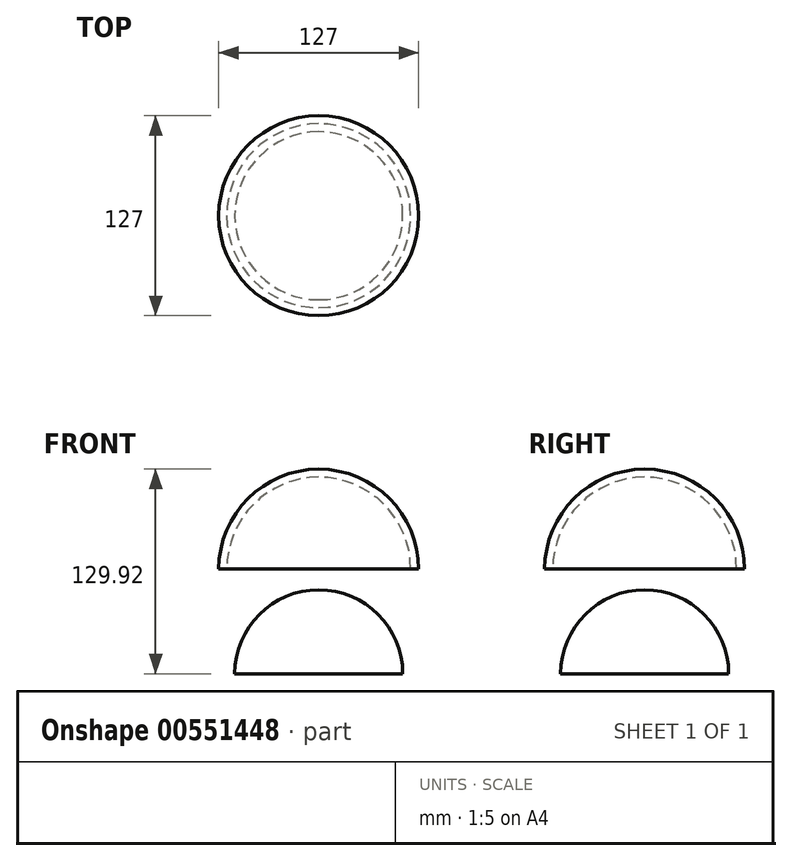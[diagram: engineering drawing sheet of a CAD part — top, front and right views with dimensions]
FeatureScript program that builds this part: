
annotation { "Feature Type Name" : "Feature", "Feature Type Description" : "" }
export const myFeature = defineFeature(function(context is Context, id is Id, definition is map)
    precondition{}
    {
        {
            var Q0;
            Q0=qCreatedBy(makeId("Top.planeOp"),FACE);
            var sketch = newSketch(context, id + "F0", { "sketchPlane" : qUnion([Q0])});
            skLineSegment(sketch, "E0", {"start": v(0, 63.5) * mm, "end": v(0, 58.42) * mm});
            skArc(sketch, "E1", {"start": v(0, 63.5) * mm, "mid": v(-63.5, 0) * mm, "end": v(0, -63.5) * mm});
            skArc(sketch, "E2", {"start": v(0, 53.34) * mm, "mid": v(-53.34, 0) * mm, "end": v(0, -53.34) * mm});
            skLineSegment(sketch, "E3", {"start": v(0, 53.34) * mm, "end": v(0, -53.34) * mm});
            skLineSegment(sketch, "E4", {"start": v(0, -53.34) * mm, "end": v(0, -58.42) * mm});
            skArc(sketch, "E5", {"start": v(0, 58.42) * mm, "mid": v(-58.42, 0) * mm, "end": v(0, -58.42) * mm});
            skLineSegment(sketch, "E6", {"start": v(0, 58.42) * mm, "end": v(0, 53.34) * mm});
            skLineSegment(sketch, "E7", {"start": v(0, -58.42) * mm, "end": v(0, -63.5) * mm});
            skSolve(sketch);
        }
        {
            var Q0;
            Q0=makeQuery(id+"F0.imprint","IMPRINT",FACE,{"disambiguationData":[TD([[makeQuery(id+"F0.imprint","IMPRINT",EDGE,{"derivedFrom":sQuery(id+"F0.wireOp",EDGE,"E2")}),1.0]])]});
            var Q1;
            Q1=sQuery(id+"F0.wireOp",EDGE,"E3");
            revolve(context, id + "F1", {"entities" : qUnion([Q0]), "axis" : qUnion([Q1]), "revolveType" : RevolveType.TWO_DIRECTIONS, "angle" : 0 * degree, "angleBack" : 180 * degree});
        }
        {
            var Q0;
            Q0=makeQuery(id+"F0.imprint","IMPRINT",FACE,{"disambiguationData":[TD([[makeQuery(id+"F0.imprint","IMPRINT",EDGE,{"derivedFrom":sQuery(id+"F0.wireOp",EDGE,"E0")}),-1.0]])]});
            var Q1;
            Q1=sQuery(id+"F0.wireOp",EDGE,"E6");
            revolve(context, id + "F2", {"entities" : qUnion([Q0]), "axis" : qUnion([Q1]), "revolveType" : RevolveType.ONE_DIRECTION, "oppositeDirection" : true, "angle" : 180 * degree});
        }
        {
            var Q0;
            Q0=qCreatedBy(makeId("Front.planeOp"),FACE);
            var sketch = newSketch(context, id + "F3", { "sketchPlane" : qUnion([Q0])});
            skLineSegment(sketch, "E8", {"start": v(0, 0) * mm, "end": v(0, 66.42) * mm});
            skSolve(sketch);
        }
        {
            var Q0;
            Q0=makeQuery(id+"F2.opRevolve","SWEPT_BODY",BODY,{"disambiguationData":[OSD([sQuery(id+"F0.wireOp",EDGE,"E0"),sQuery(id+"F0.wireOp",EDGE,"E1"),sQuery(id+"F0.wireOp",EDGE,"E5"),sQuery(id+"F0.wireOp",EDGE,"E7")])]});
            var Q1;
            Q1=sQuery(id+"F3.wireOp",EDGE,"E8");
            transform(context, id + "F4", {"entities" : qUnion([Q0]), "transformType" : TransformType.TRANSLATION_ENTITY, "oppositeDirectionEntity" : false, "transformLine" : qUnion([Q1]), "makeCopy" : false});
        }
    });
